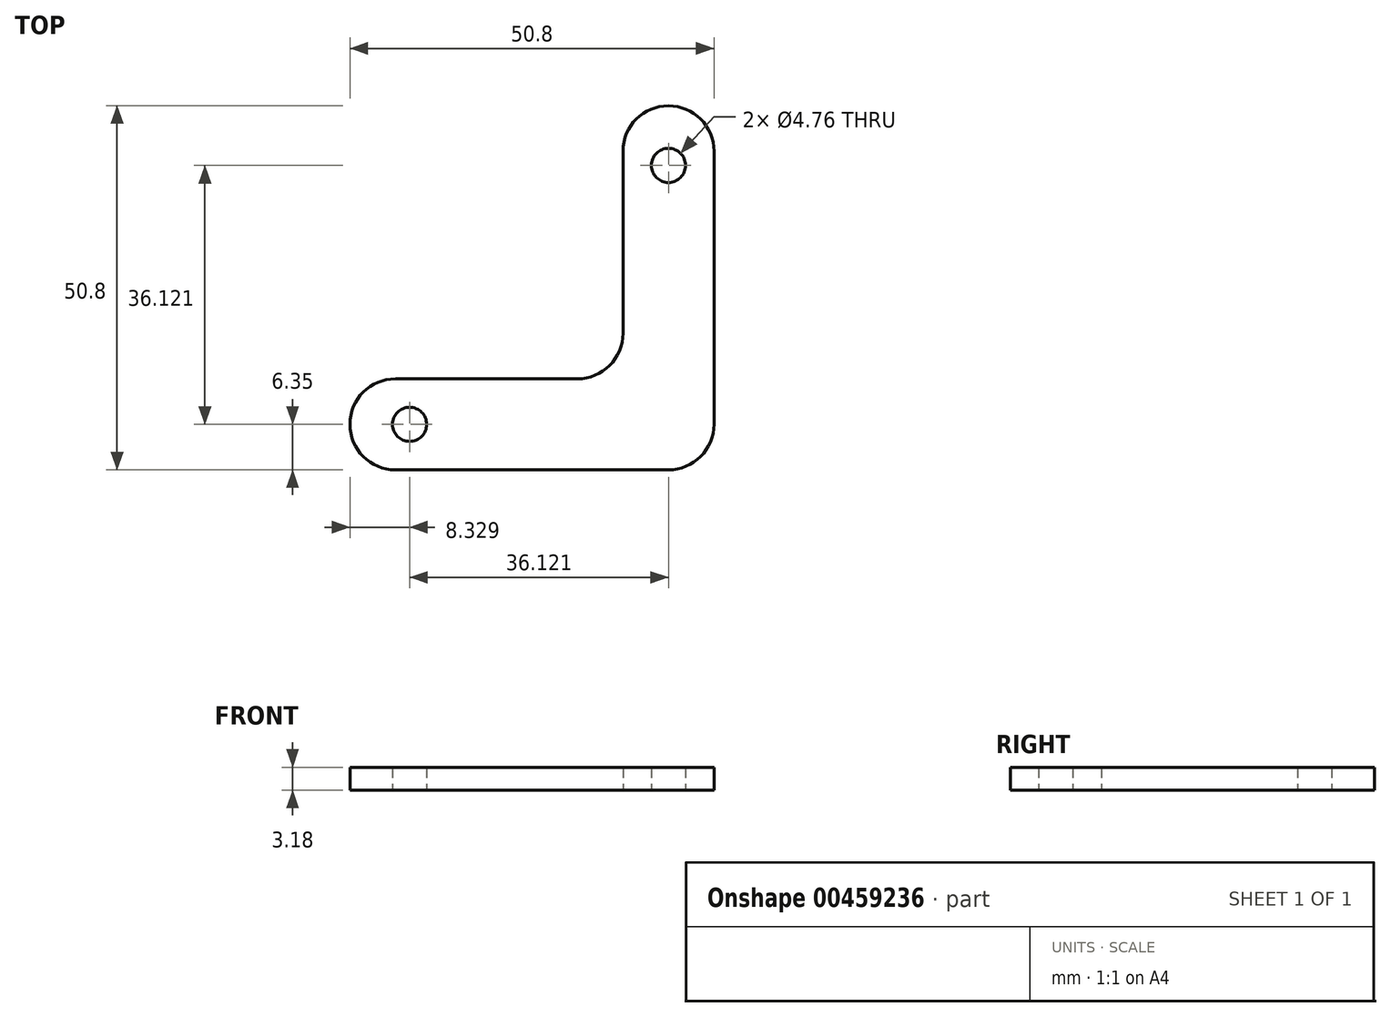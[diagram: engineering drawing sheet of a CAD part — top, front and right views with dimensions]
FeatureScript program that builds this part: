
annotation { "Feature Type Name" : "Feature", "Feature Type Description" : "" }
export const myFeature = defineFeature(function(context is Context, id is Id, definition is map)
    precondition{}
    {
        {
            var Q0;
            Q0=qCreatedBy(makeId("Top.planeOp"),FACE);
            var sketch = newSketch(context, id + "F0", { "sketchPlane" : qUnion([Q0])});
            skLineSegment(sketch, "E0", {"start": v(0, 0) * mm, "end": v(50.8, 0) * mm});
            skLineSegment(sketch, "E1", {"start": v(50.8, 0) * mm, "end": v(50.8, 50.8) * mm});
            skLineSegment(sketch, "E2", {"start": v(50.8, 50.8) * mm, "end": v(38.1, 50.8) * mm});
            skLineSegment(sketch, "E3", {"start": v(38.1, 50.8) * mm, "end": v(38.1, 12.7) * mm});
            skLineSegment(sketch, "E4", {"start": v(38.1, 12.7) * mm, "end": v(0, 12.7) * mm});
            skLineSegment(sketch, "E5", {"start": v(0, 12.7) * mm, "end": v(0, 0) * mm});
            skCircle(sketch, "E6", {"center": v(8.33, 6.35) * mm, "radius": 2.38 * mm});
            skCircle(sketch, "E7", {"center": v(44.45, 42.47) * mm, "radius": 2.38 * mm});
            skLineSegment(sketch, "E8", {"start": v(44.45, 50.8) * mm, "end": v(44.45, 42.47) * mm, "construction": true});
            skLineSegment(sketch, "E9", {"start": v(8.33, 6.35) * mm, "end": v(0, 6.35) * mm, "construction": true});
            skSolve(sketch);
        }
        {
            var Q0;
            Q0=makeQuery(id+"F0.imprint","IMPRINT",FACE,{"disambiguationData":[TD([[makeQuery(id+"F0.imprint","IMPRINT",EDGE,{"derivedFrom":sQuery(id+"F0.wireOp",EDGE,"E0")}),1.0]])]});
            extrude(context, id + "F1", {"entities" : qUnion([Q0]), "depth" : 3.17 * mm});
        }
        {
            var Q0;
            Q0=makeQuery(id+"F1.opExtrude","SWEPT_EDGE",EDGE,{"disambiguationData":[OSD([sQuery(id+"F0.wireOp",EDGE,"E0"),sQuery(id+"F0.wireOp",EDGE,"E5")])]});
            var Q1;
            Q1=makeQuery(id+"F1.opExtrude","SWEPT_EDGE",EDGE,{"disambiguationData":[OSD([sQuery(id+"F0.wireOp",EDGE,"E4"),sQuery(id+"F0.wireOp",EDGE,"E5")])]});
            var Q2;
            Q2=makeQuery(id+"F1.opExtrude","SWEPT_EDGE",EDGE,{"disambiguationData":[OSD([sQuery(id+"F0.wireOp",EDGE,"E2"),sQuery(id+"F0.wireOp",EDGE,"E3")])]});
            var Q3;
            Q3=makeQuery(id+"F1.opExtrude","SWEPT_EDGE",EDGE,{"disambiguationData":[OSD([sQuery(id+"F0.wireOp",EDGE,"E3"),sQuery(id+"F0.wireOp",EDGE,"E4")])]});
            var Q4;
            Q4=makeQuery(id+"F1.opExtrude","SWEPT_EDGE",EDGE,{"disambiguationData":[OSD([sQuery(id+"F0.wireOp",EDGE,"E0"),sQuery(id+"F0.wireOp",EDGE,"E1")])]});
            var Q5;
            Q5=makeQuery(id+"F1.opExtrude","SWEPT_EDGE",EDGE,{"disambiguationData":[OSD([sQuery(id+"F0.wireOp",EDGE,"E1"),sQuery(id+"F0.wireOp",EDGE,"E2")])]});
            fillet(context, id + "F2", {"entities" : qUnion([Q0, Q1, Q2, Q3, Q4, Q5]), "radius" : 6.35 * mm, "tangentPropagation" : true, "allowEdgeOverflow" : false});
        }
    });
